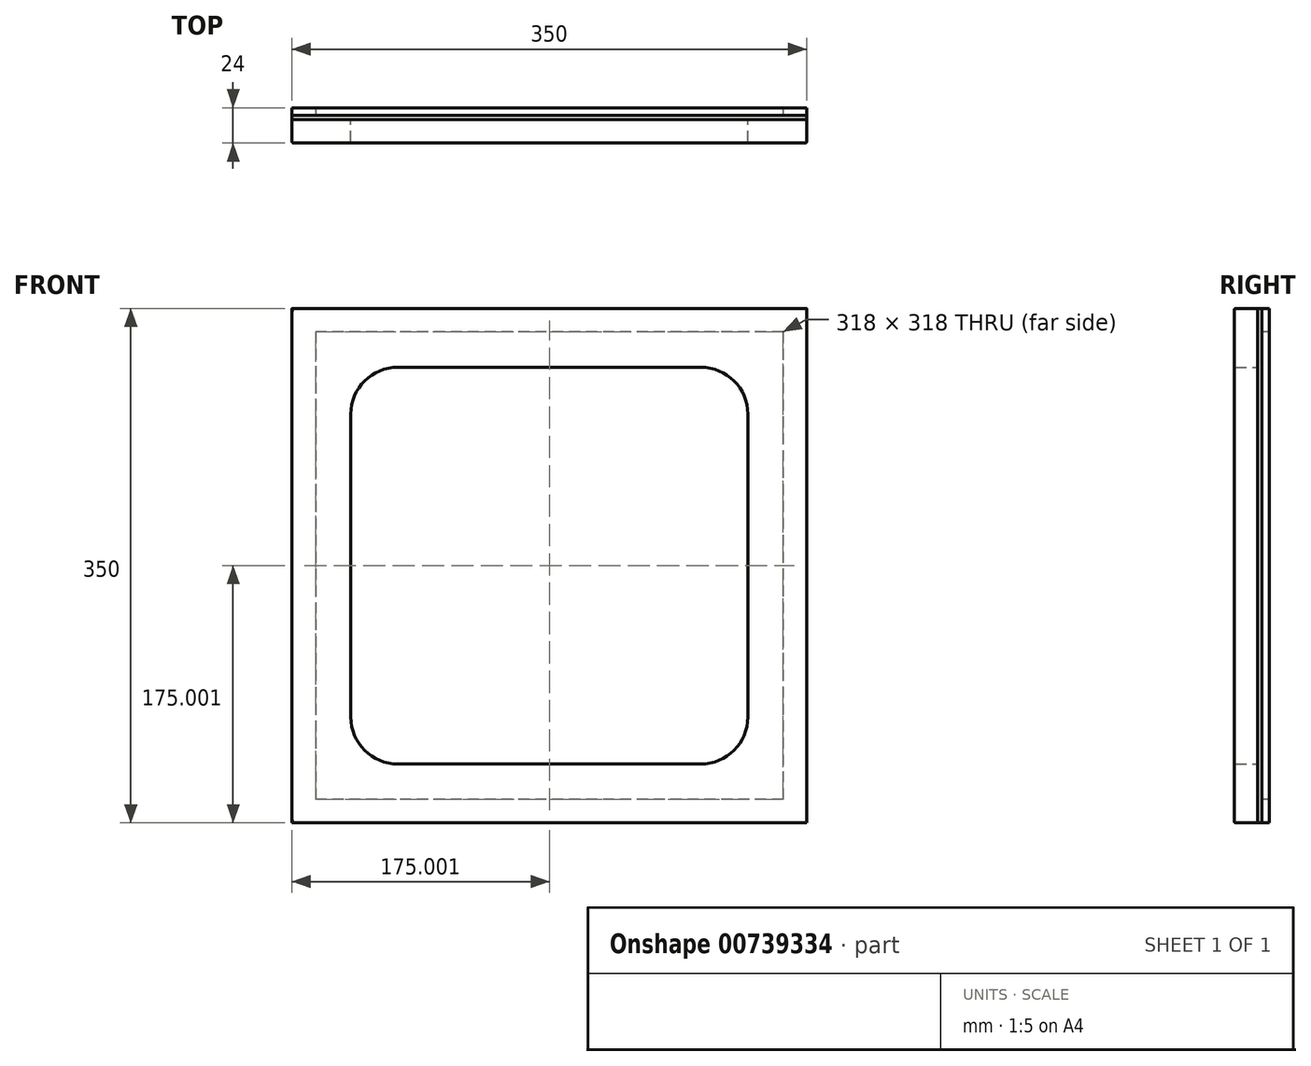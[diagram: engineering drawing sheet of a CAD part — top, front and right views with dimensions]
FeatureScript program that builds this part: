
annotation { "Feature Type Name" : "Feature", "Feature Type Description" : "" }
export const myFeature = defineFeature(function(context is Context, id is Id, definition is map)
    precondition{}
    {
        {
            var Q0;
            Q0=qCreatedBy(makeId("Front.planeOp"),FACE);
            var sketch = newSketch(context, id + "F0", { "sketchPlane" : qUnion([Q0])});
            skLineSegment(sketch, "E0.bottom", {"start": v(-167.69, 161.86) * mm, "end": v(182.31, 161.86) * mm});
            skLineSegment(sketch, "E0.top", {"start": v(-167.69, -188.14) * mm, "end": v(182.31, -188.14) * mm});
            skLineSegment(sketch, "E0.left", {"start": v(-167.69, 161.86) * mm, "end": v(-167.69, -188.14) * mm});
            skLineSegment(sketch, "E0.right", {"start": v(182.31, 161.86) * mm, "end": v(182.31, -188.14) * mm});
            skLineSegment(sketch, "E1.bottom", {"start": v(-95.69, 121.86) * mm, "end": v(110.31, 121.86) * mm});
            skLineSegment(sketch, "E1.top", {"start": v(-95.69, -148.14) * mm, "end": v(110.31, -148.14) * mm});
            skLineSegment(sketch, "E1.left", {"start": v(-127.69, 89.86) * mm, "end": v(-127.69, -116.14) * mm});
            skLineSegment(sketch, "E1.right", {"start": v(142.31, 89.86) * mm, "end": v(142.31, -116.14) * mm});
            skPoint(sketch, "E2.visualSharp", {"position": v(-127.69, 121.86) * mm});
            skArc(sketch, "E2.filletArc", {"start": v(-95.69, 121.86) * mm, "mid": v(-118.32, 112.49) * mm, "end": v(-127.69, 89.86) * mm});
            skPoint(sketch, "E3.visualSharp", {"position": v(142.31, 121.86) * mm});
            skArc(sketch, "E3.filletArc", {"start": v(142.31, 89.86) * mm, "mid": v(132.94, 112.49) * mm, "end": v(110.31, 121.86) * mm});
            skPoint(sketch, "E4.visualSharp", {"position": v(142.31, -148.14) * mm});
            skArc(sketch, "E4.filletArc", {"start": v(110.31, -148.14) * mm, "mid": v(132.94, -138.77) * mm, "end": v(142.31, -116.14) * mm});
            skPoint(sketch, "E5.visualSharp", {"position": v(-127.69, -148.14) * mm});
            skArc(sketch, "E5.filletArc", {"start": v(-127.69, -116.14) * mm, "mid": v(-118.32, -138.77) * mm, "end": v(-95.69, -148.14) * mm});
            skSolve(sketch);
        }
        {
            var Q0;
            Q0=makeQuery(id+"F0.imprint","IMPRINT",FACE,{"disambiguationData":[TD([[makeQuery(id+"F0.imprint","IMPRINT",EDGE,{"derivedFrom":sQuery(id+"F0.wireOp",EDGE,"E0.bottom")}),-1.0]])]});
            extrude(context, id + "F1", {"entities" : qUnion([Q0]), "depth" : 16 * mm, "offsetDistance" : 25 * mm});
        }
        {
            var Q0;
            Q0=makeQuery(id+"F0.imprint","IMPRINT",FACE,{"disambiguationData":[TD([[makeQuery(id+"F0.imprint","IMPRINT",EDGE,{"derivedFrom":sQuery(id+"F0.wireOp",EDGE,"E1.bottom")}),-1.0]])]});
            var Q1;
            Q1=makeQuery(id+"F0.imprint","IMPRINT",FACE,{"disambiguationData":[TD([[makeQuery(id+"F0.imprint","IMPRINT",EDGE,{"derivedFrom":sQuery(id+"F0.wireOp",EDGE,"E0.bottom")}),-1.0]])]});
            extrude(context, id + "F2", {"entities" : qUnion([Q0, Q1]), "oppositeDirection" : true, "depth" : 3 * mm, "offsetDistance" : 25 * mm});
        }
        {
            var Q0;
            Q0=makeQuery(id+"F2.opExtrude","CAP_FACE",FACE,{"disambiguationData":[OSD([sQuery(id+"F0.wireOp",EDGE,"E0.bottom"),sQuery(id+"F0.wireOp",EDGE,"E0.top"),sQuery(id+"F0.wireOp",EDGE,"E0.left"),sQuery(id+"F0.wireOp",EDGE,"E0.right")])],"isStart":false});
            var sketch = newSketch(context, id + "F3", { "sketchPlane" : qUnion([Q0])});
            skLineSegment(sketch, "E6.bottom", {"start": v(-166.31, 145.86) * mm, "end": v(151.69, 145.86) * mm});
            skLineSegment(sketch, "E6.top", {"start": v(-166.31, -172.14) * mm, "end": v(151.69, -172.14) * mm});
            skLineSegment(sketch, "E6.left", {"start": v(-166.31, 145.86) * mm, "end": v(-166.31, -172.14) * mm});
            skLineSegment(sketch, "E6.right", {"start": v(151.69, 145.86) * mm, "end": v(151.69, -172.14) * mm});
            skSolve(sketch);
        }
        {
            var Q0;
            Q0=makeQuery(id+"F3.imprint","IMPRINT",FACE,{"disambiguationData":[TD([[makeQuery(id+"F3.imprint","IMPRINT",EDGE,{"derivedFrom":sQuery(id+"F3.wireOp",EDGE,"E6.bottom")}),1.0]])]});
            extrude(context, id + "F4", {"entities" : qUnion([Q0]), "depth" : 5 * mm, "offsetDistance" : 25 * mm});
        }
        {
            var Q0;
            Q0=makeQuery(id+"F1.opExtrude","CAP_FACE",FACE,{"disambiguationData":[OSD([sQuery(id+"F0.wireOp",EDGE,"E0.bottom"),sQuery(id+"F0.wireOp",EDGE,"E0.top"),sQuery(id+"F0.wireOp",EDGE,"E0.left"),sQuery(id+"F0.wireOp",EDGE,"E0.right"),sQuery(id+"F0.wireOp",EDGE,"E1.bottom"),sQuery(id+"F0.wireOp",EDGE,"E1.top"),sQuery(id+"F0.wireOp",EDGE,"E1.left"),sQuery(id+"F0.wireOp",EDGE,"E1.right"),sQuery(id+"F0.wireOp",EDGE,"E2.filletArc"),sQuery(id+"F0.wireOp",EDGE,"E3.filletArc"),sQuery(id+"F0.wireOp",EDGE,"E4.filletArc"),sQuery(id+"F0.wireOp",EDGE,"E5.filletArc")])],"isStart":false});
            fillet(context, id + "F5", {"entities" : qUnion([Q0]), "radius" : 1 * mm, "tangentPropagation" : true, "allowEdgeOverflow" : false});
        }
    });
